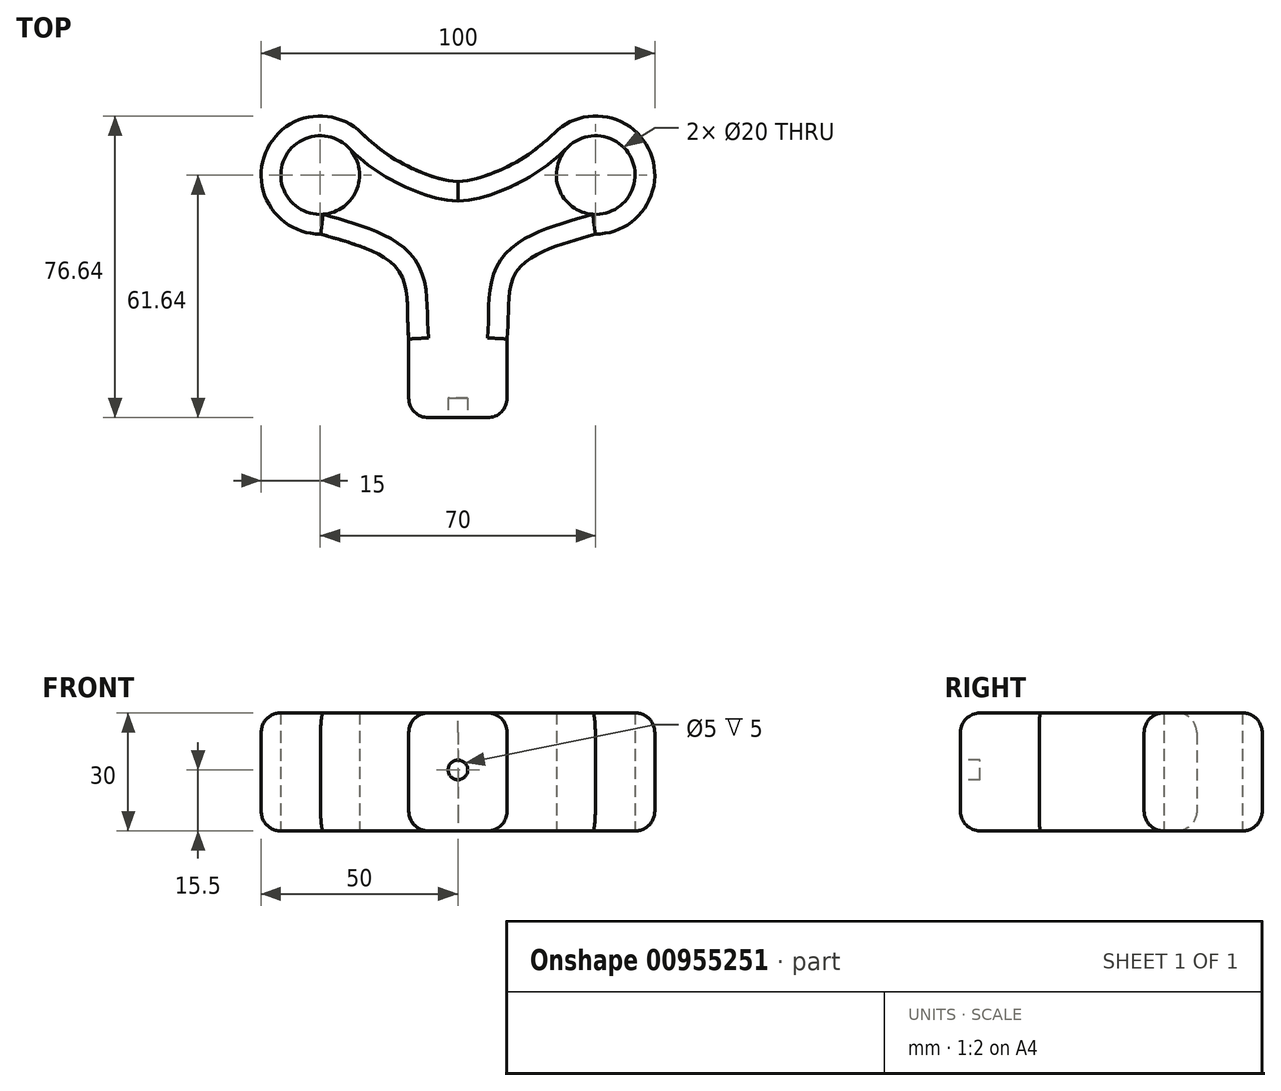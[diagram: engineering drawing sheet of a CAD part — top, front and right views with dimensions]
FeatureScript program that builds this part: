
annotation { "Feature Type Name" : "Feature", "Feature Type Description" : "" }
export const myFeature = defineFeature(function(context is Context, id is Id, definition is map)
    precondition{}
    {
        {
            var Q0;
            Q0=qCreatedBy(makeId("Top.planeOp"),FACE);
            var sketch = newSketch(context, id + "F0", { "sketchPlane" : qUnion([Q0])});
            skCircle(sketch, "E0", {"center": v(-35, 0) * mm, "radius": 10 * mm});
            skArc(sketch, "E1", {"start": v(-24.47, 10.68) * mm, "mid": v(-48.9, 5.64) * mm, "end": v(-34.9, -15) * mm});
            skFitSpline(sketch, "E2", {"points": [v(-24.47, 10.68) * mm, v(-12.43, 2.09) * mm, v(0, -1.64) * mm], "startDerivative": vector(24.17, -23.64) * mm, "endDerivative": vector(25.03, -1.32) * mm});
            skArc(sketch, "E3.MirrorC", {"start": v(24.47, 10.68) * mm, "mid": v(48.9, 5.64) * mm, "end": v(34.9, -15) * mm});
            skCircle(sketch, "E4.MirrorC", {"center": v(35, 0) * mm, "radius": 10 * mm});
            skFitSpline(sketch, "E5.MirrorCS", {"points": [v(24.47, 10.68) * mm, v(12.43, 2.09) * mm, v(0, -1.64) * mm], "startDerivative": vector(-24.17, -23.64) * mm, "endDerivative": vector(-25.03, -1.32) * mm});
            skFitSpline(sketch, "E6", {"points": [v(-34.9, -15) * mm, v(-14.97, -24.4) * mm, v(-12.5, -41.64) * mm], "startDerivative": vector(44.96, -13.06) * mm, "endDerivative": vector(4.32, -40.34) * mm});
            skFitSpline(sketch, "E7.MirrorCS", {"points": [v(34.9, -15) * mm, v(14.97, -24.4) * mm, v(12.5, -41.64) * mm], "startDerivative": vector(-44.96, -13.06) * mm, "endDerivative": vector(-4.32, -40.34) * mm});
            skLineSegment(sketch, "E8.top", {"start": v(-12.5, -61.64) * mm, "end": v(12.5, -61.64) * mm});
            skLineSegment(sketch, "E8.left", {"start": v(-12.5, -41.64) * mm, "end": v(-12.5, -61.64) * mm});
            skLineSegment(sketch, "E8.right", {"start": v(12.5, -41.64) * mm, "end": v(12.5, -61.64) * mm});
            skSolve(sketch);
        }
        {
            var Q0;
            Q0 = qSketchRegion(id + "F0", true);
            extrude(context, id + "F1", {"entities" : qUnion([Q0]), "depth" : 30 * mm, "offsetDistance" : 25 * mm});
        }
        {
            var Q0;
            Q0=makeQuery(id+"F1.opExtrude","CAP_EDGE",EDGE,{"disambiguationData":[OSD([sQuery(id+"F0.wireOp",EDGE,"E8.top")])],"isStart":false});
            fillet(context, id + "F2", {"entities" : qUnion([Q0]), "radius" : 5 * mm, "tangentPropagation" : true, "allowEdgeOverflow" : false});
        }
        {
            var Q0;
            Q0=makeQuery(id+"F1.opExtrude","CAP_EDGE",EDGE,{"disambiguationData":[OSD([sQuery(id+"F0.wireOp",EDGE,"E8.top")])],"isStart":true});
            fillet(context, id + "F3", {"entities" : qUnion([Q0]), "radius" : 5 * mm, "tangentPropagation" : true, "allowEdgeOverflow" : false});
        }
        {
            var Q0;
            Q0=makeQuery(id+"F1.opExtrude","CAP_EDGE",EDGE,{"disambiguationData":[OSD([sQuery(id+"F0.wireOp",EDGE,"E8.right")])],"isStart":false});
            fillet(context, id + "F4", {"entities" : qUnion([Q0]), "radius" : 5 * mm, "tangentPropagation" : true, "allowEdgeOverflow" : false});
        }
        {
            var Q0;
            Q0=makeQuery(id+"F1.opExtrude","CAP_EDGE",EDGE,{"disambiguationData":[OSD([sQuery(id+"F0.wireOp",EDGE,"E8.left")])],"isStart":false});
            fillet(context, id + "F5", {"entities" : qUnion([Q0]), "radius" : 5 * mm, "tangentPropagation" : true, "allowEdgeOverflow" : false});
        }
        {
            var Q0;
            Q0=makeQuery(id+"F1.opExtrude","CAP_EDGE",EDGE,{"disambiguationData":[OSD([sQuery(id+"F0.wireOp",EDGE,"E6")])],"isStart":false});
            fillet(context, id + "F6", {"entities" : qUnion([Q0]), "radius" : 5 * mm, "tangentPropagation" : true, "allowEdgeOverflow" : false});
        }
        {
            var Q0;
            Q0=makeQuery(id+"F1.opExtrude","CAP_EDGE",EDGE,{"disambiguationData":[OSD([sQuery(id+"F0.wireOp",EDGE,"E1")])],"isStart":false});
            fillet(context, id + "F7", {"entities" : qUnion([Q0]), "radius" : 5 * mm, "tangentPropagation" : true, "allowEdgeOverflow" : false});
        }
        {
            var Q0;
            Q0=makeQuery(id+"F1.opExtrude","CAP_EDGE",EDGE,{"disambiguationData":[OSD([sQuery(id+"F0.wireOp",EDGE,"E8.left")])],"isStart":false});
            fillet(context, id + "F8", {"entities" : qUnion([Q0]), "radius" : 5 * mm, "tangentPropagation" : true, "allowEdgeOverflow" : false});
        }
        {
            var Q0;
            Q0=makeQuery(id+"F1.opExtrude","CAP_EDGE",EDGE,{"disambiguationData":[OSD([sQuery(id+"F0.wireOp",EDGE,"E7.MirrorCS")])],"isStart":false});
            fillet(context, id + "F9", {"entities" : qUnion([Q0]), "radius" : 5 * mm, "tangentPropagation" : true, "allowEdgeOverflow" : false});
        }
        {
            var Q0;
            Q0=makeQuery(id+"F1.opExtrude","CAP_EDGE",EDGE,{"disambiguationData":[OSD([sQuery(id+"F0.wireOp",EDGE,"E8.right")])],"isStart":false});
            fillet(context, id + "F10", {"entities" : qUnion([Q0]), "radius" : 5 * mm, "tangentPropagation" : true, "allowEdgeOverflow" : false});
        }
        {
            var Q0;
            Q0=makeQuery(id+"F1.opExtrude","CAP_EDGE",EDGE,{"disambiguationData":[OSD([sQuery(id+"F0.wireOp",EDGE,"E3.MirrorC")])],"isStart":false});
            fillet(context, id + "F11", {"entities" : qUnion([Q0]), "radius" : 5 * mm, "tangentPropagation" : true, "allowEdgeOverflow" : false});
        }
        {
            var Q0;
            Q0=makeQuery(id+"F1.opExtrude","CAP_EDGE",EDGE,{"disambiguationData":[OSD([sQuery(id+"F0.wireOp",EDGE,"E7.MirrorCS")])],"isStart":true});
            fillet(context, id + "F12", {"entities" : qUnion([Q0]), "radius" : 5 * mm, "tangentPropagation" : true, "allowEdgeOverflow" : false});
        }
        {
            var Q0;
            Q0=makeQuery(id+"F1.opExtrude","CAP_EDGE",EDGE,{"disambiguationData":[OSD([sQuery(id+"F0.wireOp",EDGE,"E5.MirrorCS")])],"isStart":true});
            fillet(context, id + "F13", {"entities" : qUnion([Q0]), "radius" : 5 * mm, "tangentPropagation" : true, "allowEdgeOverflow" : false});
        }
        {
            var Q0;
            Q0=makeQuery(id+"F1.opExtrude","CAP_EDGE",EDGE,{"disambiguationData":[OSD([sQuery(id+"F0.wireOp",EDGE,"E3.MirrorC")])],"isStart":true});
            fillet(context, id + "F14", {"entities" : qUnion([Q0]), "radius" : 5 * mm, "tangentPropagation" : true, "allowEdgeOverflow" : false});
        }
        {
            var Q0;
            Q0=makeQuery(id+"F1.opExtrude","CAP_EDGE",EDGE,{"disambiguationData":[OSD([sQuery(id+"F0.wireOp",EDGE,"E8.right")])],"isStart":true});
            fillet(context, id + "F15", {"entities" : qUnion([Q0]), "radius" : 5 * mm, "tangentPropagation" : true, "allowEdgeOverflow" : false});
        }
        {
            var Q0;
            Q0=makeQuery(id+"F1.opExtrude","CAP_EDGE",EDGE,{"disambiguationData":[OSD([sQuery(id+"F0.wireOp",EDGE,"E6")])],"isStart":true});
            fillet(context, id + "F16", {"entities" : qUnion([Q0]), "radius" : 5 * mm, "tangentPropagation" : true, "allowEdgeOverflow" : false});
        }
        {
            var Q0;
            Q0=makeQuery(id+"F1.opExtrude","CAP_EDGE",EDGE,{"disambiguationData":[OSD([sQuery(id+"F0.wireOp",EDGE,"E8.left")])],"isStart":true});
            fillet(context, id + "F17", {"entities" : qUnion([Q0]), "radius" : 5 * mm, "tangentPropagation" : true, "allowEdgeOverflow" : false});
        }
        {
            var Q0;
            Q0=makeQuery(id+"F1.opExtrude","CAP_EDGE",EDGE,{"disambiguationData":[OSD([sQuery(id+"F0.wireOp",EDGE,"E1")])],"isStart":true});
            fillet(context, id + "F18", {"entities" : qUnion([Q0]), "radius" : 5 * mm, "tangentPropagation" : true, "allowEdgeOverflow" : false});
        }
        {
            var Q0;
            Q0=makeQuery(id+"F1.opExtrude","SWEPT_FACE",FACE,{"disambiguationData":[OSD([sQuery(id+"F0.wireOp",EDGE,"E8.top")])]});
            var sketch = newSketch(context, id + "F19", { "sketchPlane" : qUnion([Q0])});
            skCircle(sketch, "E9", {"center": v(0, 15.5) * mm, "radius": 2.5 * mm});
            skSolve(sketch);
        }
        {
            var Q0;
            Q0 = qSketchRegion(id + "F19", true);
            extrude(context, id + "F20", {"entities" : qUnion([Q0]), "operationType" : NewBodyOperationType.REMOVE, "oppositeDirection" : true, "depth" : 5 * mm, "offsetDistance" : 25 * mm});
        }
    });
